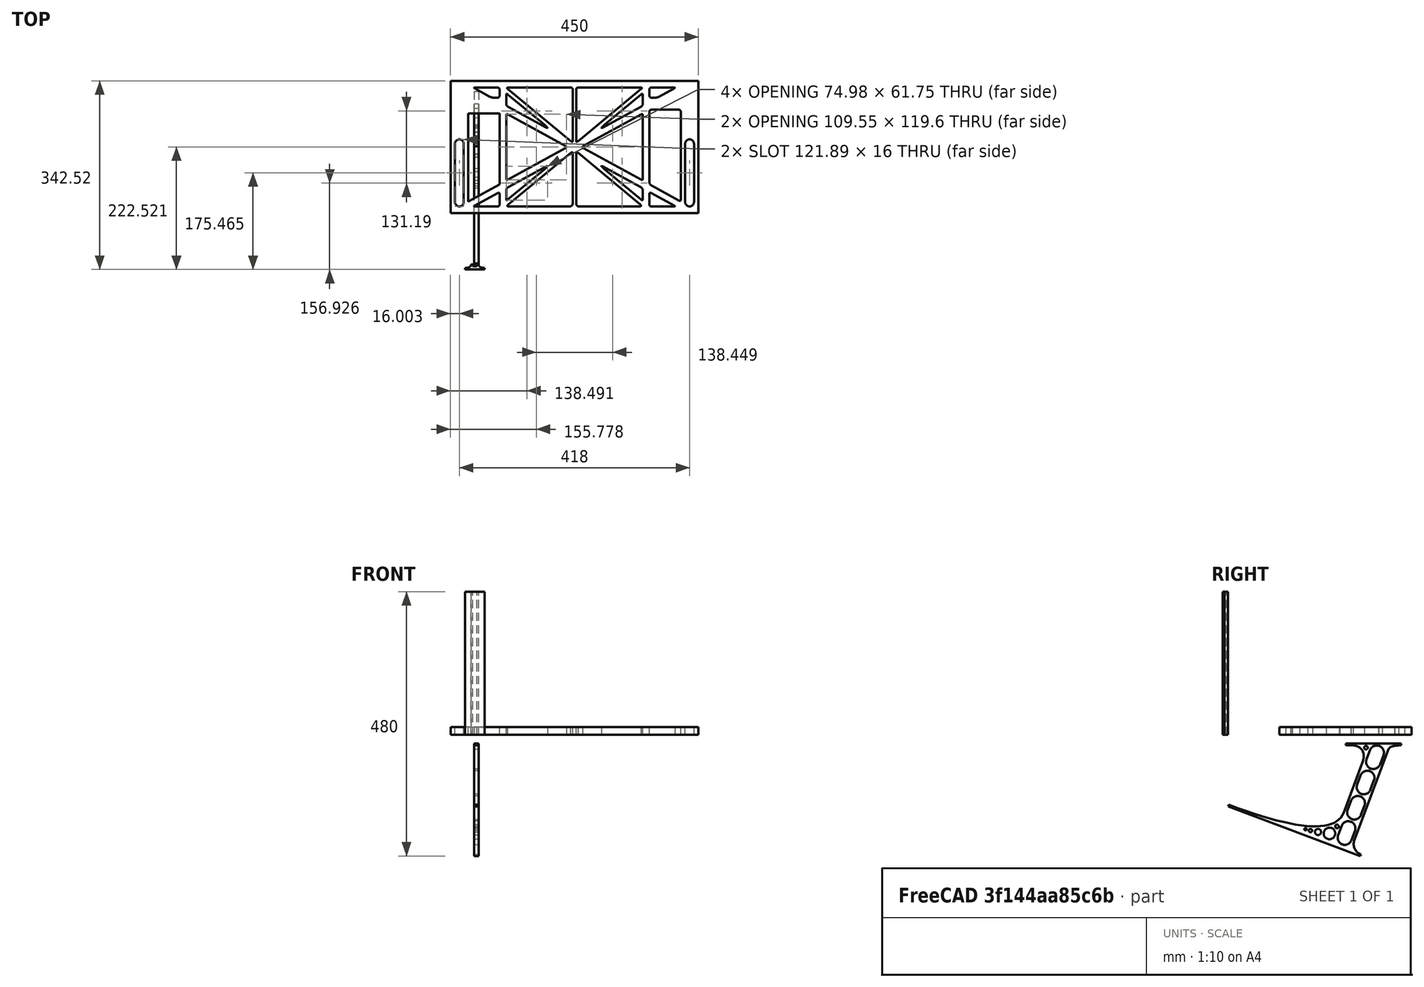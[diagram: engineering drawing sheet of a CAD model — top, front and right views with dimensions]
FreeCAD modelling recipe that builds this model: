
FCSTD DOCUMENT  (FreeCAD 0.19R0.19.2)
Label: laptopStand131FCStd
License: All rights reserved
LicenseURL: http://en.wikipedia.org/wiki/All_rights_reserved
objects: Sketcher::SketchObject×3, Part::Extrusion×3
note: 6 computed .brp shape members not serialized (recipe doc carries the construction recipe); baked Part::Feature solids carry a one-line shape summary decoded from their .brp

FEATURE [Sketcher::SketchObject] Sketch
  FullyConstrained = false
  sketch-geometry (351):
    g0: LineSegment StartX=-10.9272 StartY=-82.7794 StartZ=0 EndX=46.0728 EndY=-51.4823 EndZ=0
    g1: LineSegment StartX=-10.9272 StartY=76.4095 StartZ=0 EndX=-10.9272 EndY=-82.7794 EndZ=0
    g2: LineSegment StartX=46.0728 StartY=76.4095 StartZ=0 EndX=46.0728 EndY=-51.4823 EndZ=0
    g3: LineSegment StartX=-42.9272 StartY=136.221 StartZ=0 EndX=-42.9272 EndY=-103.779 EndZ=0
    g4: LineSegment StartX=407.073 StartY=136.221 StartZ=0 EndX=407.073 EndY=-103.779 EndZ=0
    g5: ArcOfCircle CenterX=-26.9272 CenterY=22.1087 CenterZ=0 NormalX=0 NormalY=0 NormalZ=1 AngleXU=0 Radius=8 StartAngle=1e-16 EndAngle=3.14159
    g6: ArcOfCircle CenterX=-26.9272 CenterY=-83.7794 CenterZ=0 NormalX=0 NormalY=0 NormalZ=1 AngleXU=0 Radius=8 StartAngle=3.14159 EndAngle=6.28319
    g7: LineSegment StartX=-34.9272 StartY=22.1087 StartZ=0 EndX=-34.9272 EndY=-83.7794 EndZ=0
    g8: LineSegment StartX=-18.9272 StartY=22.1087 StartZ=0 EndX=-18.9272 EndY=-83.7794 EndZ=0
    g9: ArcOfCircle CenterX=391.073 CenterY=22.1087 CenterZ=0 NormalX=0 NormalY=0 NormalZ=1 AngleXU=0 Radius=8 StartAngle=-4.4e-15 EndAngle=3.14159
    g10: LineSegment StartX=399.073 StartY=22.1087 StartZ=0 EndX=399.073 EndY=-83.7794 EndZ=0
    g11: LineSegment StartX=383.073 StartY=22.1087 StartZ=0 EndX=383.073 EndY=-83.7794 EndZ=0
    g12: ArcOfCircle CenterX=391.073 CenterY=-83.7794 CenterZ=0 NormalX=0 NormalY=0 NormalZ=1 AngleXU=0 Radius=8 StartAngle=3.14159 EndAngle=6.28319
    g13: Circle CenterX=175.022 CenterY=27.0628 CenterZ=0 NormalX=0 NormalY=0 NormalZ=1 AngleXU=0 Radius=1
    g14: Circle CenterX=179.022 CenterY=24.8665 CenterZ=0 NormalX=0 NormalY=0 NormalZ=1 AngleXU=0 Radius=1
    g15: Circle CenterX=179.022 CenterY=27.0628 CenterZ=0 NormalX=0 NormalY=0 NormalZ=1 AngleXU=0 Radius=1
    g16: BSplineCurve PolesCount=3 KnotsCount=2 Degree=2 IsPeriodic=0
    g17: GeomPoint X=175.022 Y=27.0628 Z=0
    g18: GeomPoint X=179.022 Y=27.0628 Z=0
    g19: Circle CenterX=189.124 CenterY=27.0628 CenterZ=0 NormalX=0 NormalY=0 NormalZ=1 AngleXU=0 Radius=1
    g20: Circle CenterX=185.124 CenterY=24.8665 CenterZ=0 NormalX=0 NormalY=0 NormalZ=1 AngleXU=0 Radius=1
    g21: Circle CenterX=185.124 CenterY=27.0628 CenterZ=0 NormalX=0 NormalY=0 NormalZ=1 AngleXU=0 Radius=1
    g22: BSplineCurve PolesCount=3 KnotsCount=2 Degree=2 IsPeriodic=0
    g23: GeomPoint X=189.124 Y=27.0628 Z=0
    g24: GeomPoint X=185.124 Y=27.0628 Z=0
    g25: Circle CenterX=175.022 CenterY=5.37834 CenterZ=0 NormalX=0 NormalY=0 NormalZ=1 AngleXU=0 Radius=1
    g26: Circle CenterX=179.022 CenterY=7.57463 CenterZ=0 NormalX=0 NormalY=0 NormalZ=1 AngleXU=0 Radius=1
    g27: Circle CenterX=179.022 CenterY=5.34704 CenterZ=0 NormalX=0 NormalY=0 NormalZ=1 AngleXU=0 Radius=1
    g28: BSplineCurve PolesCount=3 KnotsCount=2 Degree=2 IsPeriodic=0
    g29: GeomPoint X=175.022 Y=5.37834 Z=0
    g30: GeomPoint X=179.022 Y=5.34704 Z=0
    g31: Circle CenterX=189.124 CenterY=5.37834 CenterZ=0 NormalX=0 NormalY=0 NormalZ=1 AngleXU=0 Radius=1
    g32: Circle CenterX=185.124 CenterY=7.57463 CenterZ=0 NormalX=0 NormalY=0 NormalZ=1 AngleXU=0 Radius=1
    g33: Circle CenterX=185.124 CenterY=5.34704 CenterZ=0 NormalX=0 NormalY=0 NormalZ=1 AngleXU=0 Radius=1
    g34: BSplineCurve PolesCount=3 KnotsCount=2 Degree=2 IsPeriodic=0
    g35: GeomPoint X=189.124 Y=5.37834 Z=0
    g36: GeomPoint X=185.124 Y=5.34704 Z=0
    g37: Circle CenterX=165.871 CenterY=18.1458 CenterZ=0 NormalX=0 NormalY=0 NormalZ=1 AngleXU=0 Radius=1
    g38: Circle CenterX=169.377 CenterY=16.2206 CenterZ=0 NormalX=0 NormalY=0 NormalZ=1 AngleXU=0 Radius=1
    g39: Circle CenterX=165.871 CenterY=14.2954 CenterZ=0 NormalX=0 NormalY=0 NormalZ=1 AngleXU=0 Radius=1
    g40: BSplineCurve PolesCount=3 KnotsCount=2 Degree=2 IsPeriodic=0
    g41: GeomPoint X=165.871 Y=18.1458 Z=0
    g42: GeomPoint X=165.871 Y=14.2954 Z=0
    g43: Circle CenterX=198.275 CenterY=18.1458 CenterZ=0 NormalX=0 NormalY=0 NormalZ=1 AngleXU=0 Radius=1
    g44: Circle CenterX=194.768 CenterY=16.2206 CenterZ=0 NormalX=0 NormalY=0 NormalZ=1 AngleXU=0 Radius=1
    g45: Circle CenterX=198.275 CenterY=14.2954 CenterZ=0 NormalX=0 NormalY=0 NormalZ=1 AngleXU=0 Radius=1
    g46: BSplineCurve PolesCount=3 KnotsCount=2 Degree=2 IsPeriodic=0
    g47: GeomPoint X=198.275 Y=18.1458 Z=0
    g48: GeomPoint X=198.275 Y=14.2954 Z=0
    g49: LineSegment StartX=407.073 StartY=-103.779 StartZ=0 EndX=-42.9272 EndY=-103.779 EndZ=0
    g50: LineSegment StartX=407.073 StartY=136.221 StartZ=0 EndX=-42.9272 EndY=136.221 EndZ=0
    g51: LineSegment StartX=46.0728 StartY=76.4095 StartZ=0 EndX=-10.9272 EndY=76.4095 EndZ=0
    g52: Circle CenterX=125.607 CenterY=54.1951 CenterZ=0 NormalX=0 NormalY=0 NormalZ=1 AngleXU=0 Radius=1
    g53: Circle CenterX=139.632 CenterY=46.4944 CenterZ=0 NormalX=0 NormalY=0 NormalZ=1 AngleXU=0 Radius=1
    g54: Circle CenterX=127.326 CenterY=56.7187 CenterZ=0 NormalX=0 NormalY=0 NormalZ=1 AngleXU=0 Radius=1
    g55: BSplineCurve PolesCount=3 KnotsCount=2 Degree=2 IsPeriodic=0
    g56: GeomPoint X=125.607 Y=54.1951 Z=0
    g57: GeomPoint X=127.326 Y=56.7187 Z=0
    g58: Circle CenterX=236.821 CenterY=56.7187 CenterZ=0 NormalX=0 NormalY=0 NormalZ=1 AngleXU=0 Radius=1
    g59: Circle CenterX=224.513 CenterY=46.4944 CenterZ=0 NormalX=0 NormalY=0 NormalZ=1 AngleXU=0 Radius=1
    g60: Circle CenterX=238.538 CenterY=54.1951 CenterZ=0 NormalX=0 NormalY=0 NormalZ=1 AngleXU=0 Radius=1
    g61: BSplineCurve PolesCount=3 KnotsCount=2 Degree=2 IsPeriodic=0
    g62: GeomPoint X=236.821 Y=56.7187 Z=0
    g63: GeomPoint X=238.538 Y=54.1951 Z=0
    g64: Circle CenterX=238.538 CenterY=-21.7539 CenterZ=0 NormalX=0 NormalY=0 NormalZ=1 AngleXU=0 Radius=1
    g65: Circle CenterX=224.513 CenterY=-14.0532 CenterZ=0 NormalX=0 NormalY=0 NormalZ=1 AngleXU=0 Radius=1
    g66: Circle CenterX=236.821 CenterY=-24.2775 CenterZ=0 NormalX=0 NormalY=0 NormalZ=1 AngleXU=0 Radius=1
    g67: BSplineCurve PolesCount=3 KnotsCount=2 Degree=2 IsPeriodic=0
    g68: GeomPoint X=238.538 Y=-21.7539 Z=0
    g69: GeomPoint X=236.821 Y=-24.2775 Z=0
    g70: Circle CenterX=125.607 CenterY=-21.7539 CenterZ=0 NormalX=0 NormalY=0 NormalZ=1 AngleXU=0 Radius=1
    g71: Circle CenterX=139.632 CenterY=-14.0532 CenterZ=0 NormalX=0 NormalY=0 NormalZ=1 AngleXU=0 Radius=1
    g72: Circle CenterX=127.325 CenterY=-24.2775 CenterZ=0 NormalX=0 NormalY=0 NormalZ=1 AngleXU=0 Radius=1
    g73: BSplineCurve PolesCount=3 KnotsCount=2 Degree=2 IsPeriodic=0
    g74: GeomPoint X=125.607 Y=-21.7539 Z=0
    g75: GeomPoint X=127.325 Y=-24.2775 Z=0
    g76: Circle CenterX=302.996 CenterY=111.695 CenterZ=0 NormalX=0 NormalY=0 NormalZ=1 AngleXU=0 Radius=1
    g77: Circle CenterX=306.073 CenterY=114.251 CenterZ=0 NormalX=0 NormalY=0 NormalZ=1 AngleXU=0 Radius=1
    g78: Circle CenterX=306.073 CenterY=110.251 CenterZ=0 NormalX=0 NormalY=0 NormalZ=1 AngleXU=0 Radius=1
    g79: BSplineCurve PolesCount=3 KnotsCount=2 Degree=2 IsPeriodic=0
    g80: GeomPoint X=302.996 Y=111.695 Z=0
    g81: GeomPoint X=306.073 Y=110.251 Z=0
    g82: Circle CenterX=306.073 CenterY=95.2763 CenterZ=0 NormalX=0 NormalY=0 NormalZ=1 AngleXU=0 Radius=1
    g83: Circle CenterX=306.073 CenterY=91.2763 CenterZ=0 NormalX=0 NormalY=0 NormalZ=1 AngleXU=0 Radius=1
    g84: Circle CenterX=302.567 CenterY=89.3511 CenterZ=0 NormalX=0 NormalY=0 NormalZ=1 AngleXU=0 Radius=1
    g85: BSplineCurve PolesCount=3 KnotsCount=2 Degree=2 IsPeriodic=0
    g86: GeomPoint X=306.073 Y=95.2763 Z=0
    g87: GeomPoint X=302.567 Y=89.3511 Z=0
    g88: LineSegment StartX=306.073 StartY=110.251 StartZ=0 EndX=306.073 EndY=95.2763 EndZ=0
    g89: LineSegment StartX=302.996 StartY=111.695 StartZ=0 EndX=236.821 EndY=56.7187 EndZ=0
    g90: LineSegment StartX=238.538 StartY=54.1951 StartZ=0 EndX=302.567 EndY=89.3511 EndZ=0
    g91: Circle CenterX=61.1496 CenterY=111.695 CenterZ=0 NormalX=0 NormalY=0 NormalZ=1 AngleXU=0 Radius=1
    g92: Circle CenterX=58.0728 CenterY=114.251 CenterZ=0 NormalX=0 NormalY=0 NormalZ=1 AngleXU=0 Radius=1
    g93: Circle CenterX=58.0728 CenterY=110.251 CenterZ=0 NormalX=0 NormalY=0 NormalZ=1 AngleXU=0 Radius=1
    g94: BSplineCurve PolesCount=3 KnotsCount=2 Degree=2 IsPeriodic=0
    g95: GeomPoint X=61.1496 Y=111.695 Z=0
    g96: GeomPoint X=58.0728 Y=110.251 Z=0
    g97: Circle CenterX=61.5791 CenterY=89.3511 CenterZ=0 NormalX=0 NormalY=0 NormalZ=1 AngleXU=0 Radius=1
    g98: Circle CenterX=58.0728 CenterY=91.2763 CenterZ=0 NormalX=0 NormalY=0 NormalZ=1 AngleXU=0 Radius=1
    g99: Circle CenterX=58.0728 CenterY=95.2763 CenterZ=0 NormalX=0 NormalY=0 NormalZ=1 AngleXU=0 Radius=1
    g100: BSplineCurve PolesCount=3 KnotsCount=2 Degree=2 IsPeriodic=0
    g101: GeomPoint X=61.5791 Y=89.3511 Z=0
    g102: GeomPoint X=58.0728 Y=95.2763 Z=0
    g103: LineSegment StartX=58.0728 StartY=110.251 StartZ=0 EndX=58.0728 EndY=95.2763 EndZ=0
    g104: LineSegment StartX=61.1496 StartY=111.695 StartZ=0 EndX=127.326 EndY=56.7187 EndZ=0
    g105: LineSegment StartX=125.607 StartY=54.1951 StartZ=0 EndX=61.5791 EndY=89.3511 EndZ=0
    g106: Circle CenterX=61.5791 CenterY=-56.9099 CenterZ=0 NormalX=0 NormalY=0 NormalZ=1 AngleXU=0 Radius=1
    g107: Circle CenterX=58.0728 CenterY=-58.8351 CenterZ=0 NormalX=0 NormalY=0 NormalZ=1 AngleXU=0 Radius=1
    g108: Circle CenterX=58.0728 CenterY=-62.8351 CenterZ=0 NormalX=0 NormalY=0 NormalZ=1 AngleXU=0 Radius=1
    g109: BSplineCurve PolesCount=3 KnotsCount=2 Degree=2 IsPeriodic=0
    g110: GeomPoint X=61.5791 Y=-56.9099 Z=0
    g111: GeomPoint X=58.0728 Y=-62.8351 Z=0
    g112: Circle CenterX=58.0728 CenterY=-77.8102 CenterZ=0 NormalX=0 NormalY=0 NormalZ=1 AngleXU=0 Radius=1
    g113: Circle CenterX=58.0728 CenterY=-81.8102 CenterZ=0 NormalX=0 NormalY=0 NormalZ=1 AngleXU=0 Radius=1
    g114: Circle CenterX=61.1496 CenterY=-79.2541 CenterZ=0 NormalX=0 NormalY=0 NormalZ=1 AngleXU=0 Radius=1
    g115: BSplineCurve PolesCount=3 KnotsCount=2 Degree=2 IsPeriodic=0
    g116: GeomPoint X=58.0728 Y=-77.8102 Z=0
    g117: GeomPoint X=61.1496 Y=-79.2541 Z=0
    g118: LineSegment StartX=58.0728 StartY=-62.8351 StartZ=0 EndX=58.0728 EndY=-77.8102 EndZ=0
    g119: LineSegment StartX=61.1496 StartY=-79.2541 StartZ=0 EndX=127.325 EndY=-24.2775 EndZ=0
    g120: LineSegment StartX=125.607 StartY=-21.7539 StartZ=0 EndX=61.5791 EndY=-56.9099 EndZ=0
    g121: Circle CenterX=302.567 CenterY=-56.9099 CenterZ=0 NormalX=0 NormalY=0 NormalZ=1 AngleXU=0 Radius=1
    g122: Circle CenterX=306.073 CenterY=-58.8351 CenterZ=0 NormalX=0 NormalY=0 NormalZ=1 AngleXU=0 Radius=1
    g123: Circle CenterX=306.073 CenterY=-62.8351 CenterZ=0 NormalX=0 NormalY=0 NormalZ=1 AngleXU=0 Radius=1
    g124: BSplineCurve PolesCount=3 KnotsCount=2 Degree=2 IsPeriodic=0
    g125: GeomPoint X=302.567 Y=-56.9099 Z=0
    g126: GeomPoint X=306.073 Y=-62.8351 Z=0
    g127: Circle CenterX=302.996 CenterY=-79.2541 CenterZ=0 NormalX=0 NormalY=0 NormalZ=1 AngleXU=0 Radius=1
    g128: Circle CenterX=306.073 CenterY=-81.8102 CenterZ=0 NormalX=0 NormalY=0 NormalZ=1 AngleXU=0 Radius=1
    g129: Circle CenterX=306.073 CenterY=-77.8102 CenterZ=0 NormalX=0 NormalY=0 NormalZ=1 AngleXU=0 Radius=1
    g130: BSplineCurve PolesCount=3 KnotsCount=2 Degree=2 IsPeriodic=0
    g131: GeomPoint X=302.996 Y=-79.2541 Z=0
    g132: GeomPoint X=306.073 Y=-77.8102 Z=0
    g133: LineSegment StartX=306.073 StartY=-62.8351 StartZ=0 EndX=306.073 EndY=-77.8102 EndZ=0
    g134: LineSegment StartX=302.996 StartY=-79.2541 StartZ=0 EndX=236.821 EndY=-24.2775 EndZ=0
    g135: LineSegment StartX=238.538 StartY=-21.7539 StartZ=0 EndX=302.567 EndY=-56.9099 EndZ=0
    g136: Circle CenterX=61.6457 CenterY=-88.8112 CenterZ=0 NormalX=0 NormalY=0 NormalZ=1 AngleXU=0 Radius=1
    g137: Circle CenterX=58.0728 CenterY=-91.7794 CenterZ=0 NormalX=0 NormalY=0 NormalZ=1 AngleXU=0 Radius=1
    g138: Circle CenterX=63.9135 CenterY=-91.7794 CenterZ=0 NormalX=0 NormalY=0 NormalZ=1 AngleXU=0 Radius=1
    g139: BSplineCurve PolesCount=3 KnotsCount=2 Degree=2 IsPeriodic=0
    g140: GeomPoint X=61.6457 Y=-88.8112 Z=0
    g141: GeomPoint X=63.9135 Y=-91.7794 Z=0
    g142: Circle CenterX=179.022 CenterY=-85.8163 CenterZ=0 NormalX=0 NormalY=0 NormalZ=1 AngleXU=0 Radius=1
    g143: Circle CenterX=179.022 CenterY=-91.7794 CenterZ=0 NormalX=0 NormalY=0 NormalZ=1 AngleXU=0 Radius=1
    g144: Circle CenterX=171.895 CenterY=-91.7794 CenterZ=0 NormalX=0 NormalY=0 NormalZ=1 AngleXU=0 Radius=1
    g145: BSplineCurve PolesCount=3 KnotsCount=2 Degree=2 IsPeriodic=0
    g146: GeomPoint X=179.022 Y=-85.8163 Z=0
    g147: GeomPoint X=171.895 Y=-91.7794 Z=0
    g148: Circle CenterX=185.124 CenterY=-86.2028 CenterZ=0 NormalX=0 NormalY=0 NormalZ=1 AngleXU=0 Radius=1
    g149: Circle CenterX=185.124 CenterY=-91.7794 CenterZ=0 NormalX=0 NormalY=0 NormalZ=1 AngleXU=0 Radius=1
    g150: Circle CenterX=191.747 CenterY=-91.7794 CenterZ=0 NormalX=0 NormalY=0 NormalZ=1 AngleXU=0 Radius=1
    g151: BSplineCurve PolesCount=3 KnotsCount=2 Degree=2 IsPeriodic=0
    g152: GeomPoint X=185.124 Y=-86.2028 Z=0
    g153: GeomPoint X=191.747 Y=-91.7794 Z=0
    g154: Circle CenterX=299.888 CenterY=-86.6413 CenterZ=0 NormalX=0 NormalY=0 NormalZ=1 AngleXU=0 Radius=1
    g155: Circle CenterX=306.073 CenterY=-91.7794 CenterZ=0 NormalX=0 NormalY=0 NormalZ=1 AngleXU=0 Radius=1
    g156: Circle CenterX=298.776 CenterY=-91.7794 CenterZ=0 NormalX=0 NormalY=0 NormalZ=1 AngleXU=0 Radius=1
    g157: BSplineCurve PolesCount=3 KnotsCount=2 Degree=2 IsPeriodic=0
    g158: GeomPoint X=299.888 Y=-86.6413 Z=0
    g159: GeomPoint X=298.776 Y=-91.7794 Z=0
    g160: LineSegment StartX=189.124 StartY=5.37834 StartZ=0 EndX=299.888 EndY=-86.6413 EndZ=0
    g161: LineSegment StartX=298.776 StartY=-91.7794 StartZ=0 EndX=191.747 EndY=-91.7794 EndZ=0
    g162: LineSegment StartX=185.124 StartY=-86.2028 StartZ=0 EndX=185.124 EndY=5.34704 EndZ=0
    g163: LineSegment StartX=179.022 StartY=5.34704 StartZ=0 EndX=179.022 EndY=-85.8163 EndZ=0
    g164: LineSegment StartX=171.895 StartY=-91.7794 StartZ=0 EndX=63.9135 EndY=-91.7794 EndZ=0
    g165: LineSegment StartX=61.6457 StartY=-88.8112 StartZ=0 EndX=175.022 EndY=5.37834 EndZ=0
    g166: Circle CenterX=302.073 CenterY=124.221 CenterZ=0 NormalX=0 NormalY=0 NormalZ=1 AngleXU=0 Radius=1
    g167: Circle CenterX=306.073 CenterY=124.221 CenterZ=0 NormalX=0 NormalY=0 NormalZ=1 AngleXU=0 Radius=1
    g168: Circle CenterX=302.996 CenterY=121.665 CenterZ=0 NormalX=0 NormalY=0 NormalZ=1 AngleXU=0 Radius=1
    g169: BSplineCurve PolesCount=3 KnotsCount=2 Degree=2 IsPeriodic=0
    g170: GeomPoint X=302.073 Y=124.221 Z=0
    g171: GeomPoint X=302.996 Y=121.665 Z=0
    g172: Circle CenterX=189.124 CenterY=124.221 CenterZ=0 NormalX=0 NormalY=0 NormalZ=1 AngleXU=0 Radius=1
    g173: Circle CenterX=185.124 CenterY=124.221 CenterZ=0 NormalX=0 NormalY=0 NormalZ=1 AngleXU=0 Radius=1
    g174: Circle CenterX=185.124 CenterY=120.221 CenterZ=0 NormalX=0 NormalY=0 NormalZ=1 AngleXU=0 Radius=1
    g175: BSplineCurve PolesCount=3 KnotsCount=2 Degree=2 IsPeriodic=0
    g176: GeomPoint X=189.124 Y=124.221 Z=0
    g177: GeomPoint X=185.124 Y=120.221 Z=0
    g178: Circle CenterX=175.022 CenterY=124.221 CenterZ=0 NormalX=0 NormalY=0 NormalZ=1 AngleXU=0 Radius=1
    g179: Circle CenterX=179.022 CenterY=124.221 CenterZ=0 NormalX=0 NormalY=0 NormalZ=1 AngleXU=0 Radius=1
    g180: Circle CenterX=179.022 CenterY=120.221 CenterZ=0 NormalX=0 NormalY=0 NormalZ=1 AngleXU=0 Radius=1
    g181: BSplineCurve PolesCount=3 KnotsCount=2 Degree=2 IsPeriodic=0
    g182: GeomPoint X=175.022 Y=124.221 Z=0
    g183: GeomPoint X=179.022 Y=120.221 Z=0
    g184: Circle CenterX=62.0728 CenterY=124.221 CenterZ=0 NormalX=0 NormalY=0 NormalZ=1 AngleXU=0 Radius=1
    g185: Circle CenterX=58.0728 CenterY=124.221 CenterZ=0 NormalX=0 NormalY=0 NormalZ=1 AngleXU=0 Radius=1
    g186: Circle CenterX=61.1496 CenterY=121.665 CenterZ=0 NormalX=0 NormalY=0 NormalZ=1 AngleXU=0 Radius=1
    g187: BSplineCurve PolesCount=3 KnotsCount=2 Degree=2 IsPeriodic=0
    g188: GeomPoint X=62.0728 Y=124.221 Z=0
    g189: GeomPoint X=61.1496 Y=121.665 Z=0
    g190: LineSegment StartX=62.0728 StartY=124.221 StartZ=0 EndX=175.022 EndY=124.221 EndZ=0
    g191: LineSegment StartX=179.022 StartY=120.221 StartZ=0 EndX=179.022 EndY=27.0628 EndZ=0
    g192: LineSegment StartX=185.124 StartY=27.0628 StartZ=0 EndX=185.124 EndY=120.221 EndZ=0
    g193: LineSegment StartX=189.124 StartY=124.221 StartZ=0 EndX=302.073 EndY=124.221 EndZ=0
    g194: LineSegment StartX=302.996 StartY=121.665 StartZ=0 EndX=189.124 EndY=27.0628 EndZ=0
    g195: LineSegment StartX=175.022 StartY=27.0628 StartZ=0 EndX=61.1496 EndY=121.665 EndZ=0
    g196: Circle CenterX=61.5791 CenterY=75.4095 CenterZ=0 NormalX=0 NormalY=0 NormalZ=1 AngleXU=0 Radius=1
    g197: Circle CenterX=58.0728 CenterY=77.3346 CenterZ=0 NormalX=0 NormalY=0 NormalZ=1 AngleXU=0 Radius=1
    g198: Circle CenterX=58.0728 CenterY=73.3346 CenterZ=0 NormalX=0 NormalY=0 NormalZ=1 AngleXU=0 Radius=1
    g199: BSplineCurve PolesCount=3 KnotsCount=2 Degree=2 IsPeriodic=0
    g200: GeomPoint X=61.5791 Y=75.4095 Z=0
    g201: GeomPoint X=58.0728 Y=73.3346 Z=0
    g202: Circle CenterX=58.0728 CenterY=-40.8935 CenterZ=0 NormalX=0 NormalY=0 NormalZ=1 AngleXU=0 Radius=1
    g203: Circle CenterX=58.0728 CenterY=-44.8935 CenterZ=0 NormalX=0 NormalY=0 NormalZ=1 AngleXU=0 Radius=1
    g204: Circle CenterX=61.5791 CenterY=-42.9683 CenterZ=0 NormalX=0 NormalY=0 NormalZ=1 AngleXU=0 Radius=1
    g205: BSplineCurve PolesCount=3 KnotsCount=2 Degree=2 IsPeriodic=0
    g206: GeomPoint X=58.0728 Y=-40.8935 Z=0
    g207: GeomPoint X=61.5791 Y=-42.9683 Z=0
    g208: LineSegment StartX=61.5791 StartY=-42.9683 StartZ=0 EndX=165.871 EndY=14.2954 EndZ=0
    g209: LineSegment StartX=165.871 StartY=18.1458 StartZ=0 EndX=61.5791 EndY=75.4095 EndZ=0
    g210: LineSegment StartX=58.0728 StartY=73.3346 StartZ=0 EndX=58.0728 EndY=-40.8935 EndZ=0
    g211: Circle CenterX=302.567 CenterY=-42.9683 CenterZ=0 NormalX=0 NormalY=0 NormalZ=1 AngleXU=0 Radius=1
    g212: Circle CenterX=306.073 CenterY=-44.8935 CenterZ=0 NormalX=0 NormalY=0 NormalZ=1 AngleXU=0 Radius=1
    g213: Circle CenterX=306.073 CenterY=-40.8935 CenterZ=0 NormalX=0 NormalY=0 NormalZ=1 AngleXU=0 Radius=1
    g214: BSplineCurve PolesCount=3 KnotsCount=2 Degree=2 IsPeriodic=0
    g215: GeomPoint X=302.567 Y=-42.9683 Z=0
    g216: GeomPoint X=306.073 Y=-40.8935 Z=0
    g217: Circle CenterX=306.073 CenterY=73.3346 CenterZ=0 NormalX=0 NormalY=0 NormalZ=1 AngleXU=0 Radius=1
    g218: Circle CenterX=306.073 CenterY=77.3346 CenterZ=0 NormalX=0 NormalY=0 NormalZ=1 AngleXU=0 Radius=1
    g219: Circle CenterX=302.567 CenterY=75.4095 CenterZ=0 NormalX=0 NormalY=0 NormalZ=1 AngleXU=0 Radius=1
    g220: BSplineCurve PolesCount=3 KnotsCount=2 Degree=2 IsPeriodic=0
    g221: GeomPoint X=306.073 Y=73.3346 Z=0
    g222: GeomPoint X=302.567 Y=75.4095 Z=0
    g223: LineSegment StartX=302.567 StartY=-42.9683 StartZ=0 EndX=198.275 EndY=14.2954 EndZ=0
    g224: LineSegment StartX=198.275 StartY=18.1458 StartZ=0 EndX=302.567 EndY=75.4095 EndZ=0
    g225: LineSegment StartX=306.073 StartY=73.3346 StartZ=0 EndX=306.073 EndY=-40.8935 EndZ=0
    g226: LineSegment StartX=322.073 StartY=105.865 StartZ=0 EndX=328.643 EndY=105.865 EndZ=0
    g227: LineSegment StartX=318.073 StartY=120.221 StartZ=0 EndX=318.073 EndY=109.865 EndZ=0
    g228: LineSegment StartX=336.157 StartY=107.779 StartZ=0 EndX=362.567 EndY=122.294 EndZ=0
    g229: Circle CenterX=362.073 CenterY=124.221 CenterZ=0 NormalX=0 NormalY=0 NormalZ=1 AngleXU=0 Radius=1
    g230: Circle CenterX=366.073 CenterY=124.221 CenterZ=0 NormalX=0 NormalY=0 NormalZ=1 AngleXU=0 Radius=1
    g231: Circle CenterX=362.567 CenterY=122.294 CenterZ=0 NormalX=0 NormalY=0 NormalZ=1 AngleXU=0 Radius=1
    g232: BSplineCurve PolesCount=3 KnotsCount=2 Degree=2 IsPeriodic=0
    g233: GeomPoint X=362.073 Y=124.221 Z=0
    g234: GeomPoint X=362.567 Y=122.294 Z=0
    g235: Circle CenterX=322.073 CenterY=124.221 CenterZ=0 NormalX=0 NormalY=0 NormalZ=1 AngleXU=0 Radius=1
    g236: Circle CenterX=318.073 CenterY=124.221 CenterZ=0 NormalX=0 NormalY=0 NormalZ=1 AngleXU=0 Radius=1
    g237: Circle CenterX=318.073 CenterY=120.221 CenterZ=0 NormalX=0 NormalY=0 NormalZ=1 AngleXU=0 Radius=1
    g238: BSplineCurve PolesCount=3 KnotsCount=2 Degree=2 IsPeriodic=0
    g239: GeomPoint X=322.073 Y=124.221 Z=0
    g240: GeomPoint X=318.073 Y=120.221 Z=0
    g241: Circle CenterX=322.073 CenterY=105.865 CenterZ=0 NormalX=0 NormalY=0 NormalZ=1 AngleXU=0 Radius=1
    g242: Circle CenterX=318.073 CenterY=105.865 CenterZ=0 NormalX=0 NormalY=0 NormalZ=1 AngleXU=0 Radius=1
    g243: Circle CenterX=318.073 CenterY=109.865 CenterZ=0 NormalX=0 NormalY=0 NormalZ=1 AngleXU=0 Radius=1
    g244: BSplineCurve PolesCount=3 KnotsCount=2 Degree=2 IsPeriodic=0
    g245: GeomPoint X=322.073 Y=105.865 Z=0
    g246: GeomPoint X=318.073 Y=109.865 Z=0
    g247: Circle CenterX=336.157 CenterY=107.779 CenterZ=0 NormalX=0 NormalY=0 NormalZ=1 AngleXU=0 Radius=1
    g248: Circle CenterX=332.651 CenterY=105.853 CenterZ=0 NormalX=0 NormalY=0 NormalZ=1 AngleXU=0 Radius=1
    g249: Circle CenterX=328.643 CenterY=105.865 CenterZ=0 NormalX=0 NormalY=0 NormalZ=1 AngleXU=0 Radius=1
    g250: BSplineCurve PolesCount=3 KnotsCount=2 Degree=2 IsPeriodic=0
    g251: GeomPoint X=336.157 Y=107.779 Z=0
    g252: GeomPoint X=328.643 Y=105.865 Z=0
    g253: LineSegment StartX=322.073 StartY=124.221 StartZ=0 EndX=362.073 EndY=124.221 EndZ=0
    g254: Circle CenterX=371.567 CenterY=-80.8644 CenterZ=0 NormalX=0 NormalY=0 NormalZ=1 AngleXU=0 Radius=1
    g255: Circle CenterX=375.073 CenterY=-82.7896 CenterZ=0 NormalX=0 NormalY=0 NormalZ=1 AngleXU=0 Radius=1
    g256: Circle CenterX=375.073 CenterY=-78.7896 CenterZ=0 NormalX=0 NormalY=0 NormalZ=1 AngleXU=0 Radius=1
    g257: BSplineCurve PolesCount=3 KnotsCount=2 Degree=2 IsPeriodic=0
    g258: GeomPoint X=371.567 Y=-80.8644 Z=0
    g259: GeomPoint X=375.073 Y=-78.7896 Z=0
    g260: Circle CenterX=321.579 CenterY=-53.4075 CenterZ=0 NormalX=0 NormalY=0 NormalZ=1 AngleXU=0 Radius=1
    g261: Circle CenterX=318.073 CenterY=-51.4823 CenterZ=0 NormalX=0 NormalY=0 NormalZ=1 AngleXU=0 Radius=1
    g262: Circle CenterX=318.073 CenterY=-47.4823 CenterZ=0 NormalX=0 NormalY=0 NormalZ=1 AngleXU=0 Radius=1
    g263: BSplineCurve PolesCount=3 KnotsCount=2 Degree=2 IsPeriodic=0
    g264: GeomPoint X=321.579 Y=-53.4075 Z=0
    g265: GeomPoint X=318.073 Y=-47.4823 Z=0
    g266: Circle CenterX=375.073 CenterY=79.9235 CenterZ=0 NormalX=0 NormalY=0 NormalZ=1 AngleXU=0 Radius=1
    g267: Circle CenterX=375.073 CenterY=83.9235 CenterZ=0 NormalX=0 NormalY=0 NormalZ=1 AngleXU=0 Radius=1
    g268: Circle CenterX=371.073 CenterY=83.9235 CenterZ=0 NormalX=0 NormalY=0 NormalZ=1 AngleXU=0 Radius=1
    g269: BSplineCurve PolesCount=3 KnotsCount=2 Degree=2 IsPeriodic=0
    g270: GeomPoint X=375.073 Y=79.9235 Z=0
    g271: GeomPoint X=371.073 Y=83.9235 Z=0
    g272: LineSegment StartX=371.567 StartY=-80.8644 StartZ=0 EndX=321.579 EndY=-53.4075 EndZ=0
    g273: LineSegment StartX=318.073 StartY=-47.4823 StartZ=0 EndX=318.073 EndY=76.4095 EndZ=0
    g274: Circle CenterX=321.579 CenterY=-67.3492 CenterZ=0 NormalX=0 NormalY=0 NormalZ=1 AngleXU=0 Radius=1
    g275: Circle CenterX=318.073 CenterY=-65.424 CenterZ=0 NormalX=0 NormalY=0 NormalZ=1 AngleXU=0 Radius=1
    g276: Circle CenterX=318.073 CenterY=-69.424 CenterZ=0 NormalX=0 NormalY=0 NormalZ=1 AngleXU=0 Radius=1
    g277: BSplineCurve PolesCount=3 KnotsCount=2 Degree=2 IsPeriodic=0
    g278: GeomPoint X=321.579 Y=-67.3492 Z=0
    g279: GeomPoint X=318.073 Y=-69.424 Z=0
    g280: Circle CenterX=362.567 CenterY=-89.8542 CenterZ=0 NormalX=0 NormalY=0 NormalZ=1 AngleXU=0 Radius=1
    g281: Circle CenterX=366.073 CenterY=-91.7794 CenterZ=0 NormalX=0 NormalY=0 NormalZ=1 AngleXU=0 Radius=1
    g282: Circle CenterX=362.073 CenterY=-91.7794 CenterZ=0 NormalX=0 NormalY=0 NormalZ=1 AngleXU=0 Radius=1
    g283: BSplineCurve PolesCount=3 KnotsCount=2 Degree=2 IsPeriodic=0
    g284: GeomPoint X=362.567 Y=-89.8542 Z=0
    g285: GeomPoint X=362.073 Y=-91.7794 Z=0
    g286: Circle CenterX=322.073 CenterY=-91.7794 CenterZ=0 NormalX=0 NormalY=0 NormalZ=1 AngleXU=0 Radius=1
    g287: Circle CenterX=318.073 CenterY=-91.7794 CenterZ=0 NormalX=0 NormalY=0 NormalZ=1 AngleXU=0 Radius=1
    g288: Circle CenterX=318.073 CenterY=-87.7794 CenterZ=0 NormalX=0 NormalY=0 NormalZ=1 AngleXU=0 Radius=1
    g289: BSplineCurve PolesCount=3 KnotsCount=2 Degree=2 IsPeriodic=0
    g290: GeomPoint X=322.073 Y=-91.7794 Z=0
    g291: GeomPoint X=318.073 Y=-87.7794 Z=0
    g292: LineSegment StartX=362.567 StartY=-89.8542 StartZ=0 EndX=321.579 EndY=-67.3492 EndZ=0
    g293: LineSegment StartX=318.073 StartY=-69.424 StartZ=0 EndX=318.073 EndY=-87.7794 EndZ=0
    g294: LineSegment StartX=322.073 StartY=-91.7794 StartZ=0 EndX=362.073 EndY=-91.7794 EndZ=0
    g295: Circle CenterX=2.07281 CenterY=124.221 CenterZ=0 NormalX=0 NormalY=0 NormalZ=1 AngleXU=0 Radius=1
    g296: Circle CenterX=1.57905 CenterY=122.295 CenterZ=0 NormalX=0 NormalY=0 NormalZ=1 AngleXU=0 Radius=1
    g297: BSplineCurve PolesCount=3 KnotsCount=2 Degree=2 IsPeriodic=0
    g298: GeomPoint X=2.07281 Y=124.221 Z=0
    g299: GeomPoint X=1.57905 Y=122.295 Z=0
    g300: Circle CenterX=42.0728 CenterY=124.221 CenterZ=0 NormalX=0 NormalY=0 NormalZ=1 AngleXU=0 Radius=1
    g301: Circle CenterX=46.0728 CenterY=124.221 CenterZ=0 NormalX=0 NormalY=0 NormalZ=1 AngleXU=0 Radius=1
    g302: Circle CenterX=46.0728 CenterY=120.221 CenterZ=0 NormalX=0 NormalY=0 NormalZ=1 AngleXU=0 Radius=1
    g303: BSplineCurve PolesCount=3 KnotsCount=2 Degree=2 IsPeriodic=0
    g304: GeomPoint X=42.0728 Y=124.221 Z=0
    g305: GeomPoint X=46.0728 Y=120.221 Z=0
    g306: Circle CenterX=46.0728 CenterY=109.865 CenterZ=0 NormalX=0 NormalY=0 NormalZ=1 AngleXU=0 Radius=1
    g307: Circle CenterX=46.0728 CenterY=105.865 CenterZ=0 NormalX=0 NormalY=0 NormalZ=1 AngleXU=0 Radius=1
    g308: Circle CenterX=42.0728 CenterY=105.865 CenterZ=0 NormalX=0 NormalY=0 NormalZ=1 AngleXU=0 Radius=1
    g309: BSplineCurve PolesCount=3 KnotsCount=2 Degree=2 IsPeriodic=0
    g310: GeomPoint X=46.0728 Y=109.865 Z=0
    g311: GeomPoint X=42.0728 Y=105.865 Z=0
    g312: Circle CenterX=35.5028 CenterY=105.865 CenterZ=0 NormalX=0 NormalY=0 NormalZ=1 AngleXU=0 Radius=1
    g313: Circle CenterX=31.5028 CenterY=105.865 CenterZ=0 NormalX=0 NormalY=0 NormalZ=1 AngleXU=0 Radius=1
    g314: Circle CenterX=27.9965 CenterY=107.79 CenterZ=0 NormalX=0 NormalY=0 NormalZ=1 AngleXU=0 Radius=1
    g315: BSplineCurve PolesCount=3 KnotsCount=2 Degree=2 IsPeriodic=0
    g316: GeomPoint X=35.5028 Y=105.865 Z=0
    g317: GeomPoint X=27.9965 Y=107.79 Z=0
    g318: LineSegment StartX=2.07281 StartY=124.221 StartZ=0 EndX=42.0728 EndY=124.221 EndZ=0
    g319: LineSegment StartX=46.0728 StartY=120.221 StartZ=0 EndX=46.0728 EndY=109.865 EndZ=0
    g320: LineSegment StartX=42.0728 StartY=105.865 StartZ=0 EndX=35.5028 EndY=105.865 EndZ=0
    g321: LineSegment StartX=27.9965 StartY=107.79 StartZ=0 EndX=1.57905 EndY=122.295 EndZ=0
    g322: Circle CenterX=42.5666 CenterY=-67.3492 CenterZ=0 NormalX=0 NormalY=0 NormalZ=1 AngleXU=0 Radius=1
    g323: Circle CenterX=46.0728 CenterY=-65.424 CenterZ=0 NormalX=0 NormalY=0 NormalZ=1 AngleXU=0 Radius=1
    g324: Circle CenterX=46.0728 CenterY=-69.424 CenterZ=0 NormalX=0 NormalY=0 NormalZ=1 AngleXU=0 Radius=1
    g325: BSplineCurve PolesCount=3 KnotsCount=2 Degree=2 IsPeriodic=0
    g326: GeomPoint X=42.5666 Y=-67.3492 Z=0
    g327: GeomPoint X=46.0728 Y=-69.424 Z=0
    g328: Circle CenterX=46.0728 CenterY=-87.7794 CenterZ=0 NormalX=0 NormalY=0 NormalZ=1 AngleXU=0 Radius=1
    g329: Circle CenterX=46.0728 CenterY=-91.7794 CenterZ=0 NormalX=0 NormalY=0 NormalZ=1 AngleXU=0 Radius=1
    g330: Circle CenterX=42.0728 CenterY=-91.7794 CenterZ=0 NormalX=0 NormalY=0 NormalZ=1 AngleXU=0 Radius=1
    g331: BSplineCurve PolesCount=3 KnotsCount=2 Degree=2 IsPeriodic=0
    g332: GeomPoint X=46.0728 Y=-87.7794 Z=0
    g333: GeomPoint X=42.0728 Y=-91.7794 Z=0
    g334: Circle CenterX=2.07281 CenterY=-91.7794 CenterZ=0 NormalX=0 NormalY=0 NormalZ=1 AngleXU=0 Radius=1
    g335: Circle CenterX=-1.92719 CenterY=-91.7794 CenterZ=0 NormalX=0 NormalY=0 NormalZ=1 AngleXU=0 Radius=1
    g336: Circle CenterX=1.57905 CenterY=-89.8542 CenterZ=0 NormalX=0 NormalY=0 NormalZ=1 AngleXU=0 Radius=1
    g337: BSplineCurve PolesCount=3 KnotsCount=2 Degree=2 IsPeriodic=0
    g338: GeomPoint X=2.07281 Y=-91.7794 Z=0
    g339: GeomPoint X=1.57905 Y=-89.8542 Z=0
    g340: LineSegment StartX=2.07281 StartY=-91.7794 StartZ=0 EndX=42.0728 EndY=-91.7794 EndZ=0
    g341: LineSegment StartX=46.0728 StartY=-87.7794 StartZ=0 EndX=46.0728 EndY=-69.424 EndZ=0
    g342: LineSegment StartX=42.5666 StartY=-67.3492 StartZ=0 EndX=1.57905 EndY=-89.8542 EndZ=0
    g343: LineSegment StartX=318.073 StartY=76.4095 StartZ=0 EndX=375.073 EndY=76.4095 EndZ=0
    g344: LineSegment StartX=375.073 StartY=76.4095 StartZ=0 EndX=375.073 EndY=-78.7896 EndZ=0
    g345: LineSegment StartX=318.073 StartY=76.4095 StartZ=0 EndX=322.073 EndY=76.4095 EndZ=0
    g346: Circle CenterX=322.073 CenterY=76.4095 CenterZ=0 NormalX=0 NormalY=0 NormalZ=1 AngleXU=0 Radius=1
    g347: BSplineCurve PolesCount=3 KnotsCount=2 Degree=2 IsPeriodic=0
    g348: GeomPoint X=318.073 Y=72.4095 Z=0
    g349: GeomPoint X=322.073 Y=76.4095 Z=0
    g350: LineSegment StartX=370.522 StartY=78.4793 StartZ=0 EndX=374.522 EndY=78.4793 EndZ=0
  constraints (580):
    c: Coincident(g0,g2)
    c: Block(g0)
    c: Block(g1)
    c: Vertical(g3)
    c: Vertical(g4)
    c: Block(g4)
    c: Block(g3)
    c: Tangent(g5,g8) = 1.5708
    c: Tangent(g5,g7) = -1.5708
    c: Tangent(g7,g6) = -1.5708
    c: Tangent(g8,g6) = 1.5708
    c: Vertical(g7)
    c: Equal(g5,g6)
    c: Block(g8)
    c: Block(g7)
    c: Tangent(g9,g10) = 1.5708
    c: Tangent(g10,g12) = 1.5708
    c: Equal(g9,g12)
    c: Coincident(g11,g9)
    c: Coincident(g11,g12)
    c: Block(g10)
    c: Block(g11)
    c: Weight(g13) = 1
    c: Equal(g13,g14)
    c: Equal(g13,g15)
    c: InternalAlignment(g13,g16)
    c: InternalAlignment(g14,g16)
    c: InternalAlignment(g15,g16)
    c: InternalAlignment(g17,g16)
    c: InternalAlignment(g18,g16)
    c: Weight(g19) = 1
    c: Equal(g19,g20)
    c: Equal(g19,g21)
    c: InternalAlignment(g19,g22)
    c: InternalAlignment(g20,g22)
    c: InternalAlignment(g21,g22)
    c: InternalAlignment(g23,g22)
    c: InternalAlignment(g24,g22)
    c: Block(g22)
    c: Block(g16)
    c: Weight(g25) = 1
    c: Equal(g25,g26)
    c: Equal(g25,g27)
    c: InternalAlignment(g25,g28)
    c: InternalAlignment(g26,g28)
    c: InternalAlignment(g27,g28)
    c: InternalAlignment(g29,g28)
    c: InternalAlignment(g30,g28)
    c: Weight(g31) = 1
    c: Equal(g31,g32)
    c: Equal(g31,g33)
    c: InternalAlignment(g31,g34)
    c: InternalAlignment(g32,g34)
    c: InternalAlignment(g33,g34)
    c: InternalAlignment(g35,g34)
    c: InternalAlignment(g36,g34)
    c: Block(g34)
    c: Block(g28)
    c: Weight(g37) = 1
    c: Equal(g37,g38)
    c: Equal(g37,g39)
    c: InternalAlignment(g37,g40)
    c: InternalAlignment(g38,g40)
    c: InternalAlignment(g39,g40)
    c: InternalAlignment(g41,g40)
    c: InternalAlignment(g42,g40)
    c: Weight(g43) = 1
    c: Equal(g43,g44)
    c: Equal(g43,g45)
    c: InternalAlignment(g43,g46)
    c: InternalAlignment(g44,g46)
    c: InternalAlignment(g45,g46)
    c: InternalAlignment(g47,g46)
    c: InternalAlignment(g48,g46)
    c: Block(g40)
    c: Block(g46)
    c: Coincident(g49,g4)
    c: Coincident(g49,g3)
    c: Horizontal(g49)
    c: Distance(g49) = 450
    c: Coincident(g50,g4)
    c: Coincident(g50,g3)
    c: Horizontal(g50)
    c: Horizontal(g51)
    c: Coincident(g2,g51)
    c: Block(g51)
    c: Coincident(g1,g51)
    c: Weight(g52) = 1
    c: Equal(g52,g53)
    c: Equal(g52,g54)
    c: InternalAlignment(g52,g55)
    c: InternalAlignment(g53,g55)
    c: InternalAlignment(g54,g55)
    c: InternalAlignment(g56,g55)
    c: InternalAlignment(g57,g55)
    c: Block(g55)
    c: Weight(g58) = 1
    c: Equal(g58,g59)
    c: Equal(g58,g60)
    c: InternalAlignment(g58,g61)
    c: InternalAlignment(g59,g61)
    c: InternalAlignment(g60,g61)
    c: InternalAlignment(g62,g61)
    c: InternalAlignment(g63,g61)
    c: Block(g61)
    c: Weight(g64) = 1
    c: Equal(g64,g65)
    c: Equal(g64,g66)
    c: InternalAlignment(g64,g67)
    c: InternalAlignment(g65,g67)
    c: InternalAlignment(g66,g67)
    c: InternalAlignment(g68,g67)
    c: InternalAlignment(g69,g67)
    c: Block(g67)
    c: Weight(g70) = 1
    c: Equal(g70,g71)
    c: Equal(g70,g72)
    c: InternalAlignment(g70,g73)
    c: InternalAlignment(g71,g73)
    c: InternalAlignment(g72,g73)
    c: InternalAlignment(g74,g73)
    c: InternalAlignment(g75,g73)
    c: Block(g73)
    c: Weight(g76) = 1
    c: Equal(g76,g77)
    c: Equal(g76,g78)
    c: InternalAlignment(g76,g79)
    c: InternalAlignment(g77,g79)
    c: InternalAlignment(g78,g79)
    c: InternalAlignment(g80,g79)
    c: InternalAlignment(g81,g79)
    c: Weight(g82) = 1
    c: Equal(g82,g83)
    c: Equal(g82,g84)
    c: InternalAlignment(g82,g85)
    c: InternalAlignment(g83,g85)
    c: InternalAlignment(g84,g85)
    c: InternalAlignment(g86,g85)
    c: InternalAlignment(g87,g85)
    c: Block(g79)
    c: Block(g85)
    c: Coincident(g88,g79)
    c: Coincident(g88,g85)
    c: Vertical(g88)
    c: Coincident(g89,g79)
    c: Coincident(g89,g61)
    c: Coincident(g90,g61)
    c: Coincident(g90,g85)
    c: Weight(g91) = 1
    c: Equal(g91,g92)
    c: Equal(g91,g93)
    c: InternalAlignment(g91,g94)
    c: InternalAlignment(g92,g94)
    c: InternalAlignment(g93,g94)
    c: InternalAlignment(g95,g94)
    c: InternalAlignment(g96,g94)
    c: Weight(g97) = 1
    c: Equal(g97,g98)
    c: Equal(g97,g99)
    c: InternalAlignment(g97,g100)
    c: InternalAlignment(g98,g100)
    c: InternalAlignment(g99,g100)
    c: InternalAlignment(g101,g100)
    c: InternalAlignment(g102,g100)
    c: Block(g94)
    c: Block(g100)
    c: Coincident(g103,g94)
    c: Coincident(g103,g100)
    c: Vertical(g103)
    c: Coincident(g104,g94)
    c: Coincident(g104,g55)
    c: Coincident(g105,g55)
    c: Coincident(g105,g100)
    c: Weight(g106) = 1
    c: Equal(g106,g107)
    c: Equal(g106,g108)
    c: InternalAlignment(g106,g109)
    c: InternalAlignment(g107,g109)
    c: InternalAlignment(g108,g109)
    c: InternalAlignment(g110,g109)
    c: InternalAlignment(g111,g109)
    c: Weight(g112) = 1
    c: Equal(g112,g113)
    c: Equal(g112,g114)
    c: InternalAlignment(g112,g115)
    c: InternalAlignment(g113,g115)
    c: InternalAlignment(g114,g115)
    c: InternalAlignment(g116,g115)
    c: InternalAlignment(g117,g115)
    c: Block(g109)
    c: Block(g115)
    c: Coincident(g118,g109)
    c: Coincident(g118,g115)
    c: Vertical(g118)
    c: Coincident(g119,g115)
    c: Coincident(g119,g73)
    c: Coincident(g120,g73)
    c: Coincident(g120,g109)
    c: Weight(g121) = 1
    c: Equal(g121,g122)
    c: Equal(g121,g123)
    c: InternalAlignment(g121,g124)
    c: InternalAlignment(g122,g124)
    c: InternalAlignment(g123,g124)
    c: InternalAlignment(g125,g124)
    c: InternalAlignment(g126,g124)
    c: Weight(g127) = 1
    c: Equal(g127,g128)
    c: Equal(g127,g129)
    c: InternalAlignment(g127,g130)
    c: InternalAlignment(g128,g130)
    c: InternalAlignment(g129,g130)
    c: InternalAlignment(g131,g130)
    c: InternalAlignment(g132,g130)
    c: Block(g124)
    c: Block(g130)
    c: Coincident(g133,g124)
    c: Coincident(g133,g130)
    c: Vertical(g133)
    c: Coincident(g134,g130)
    c: Coincident(g134,g67)
    c: Coincident(g135,g67)
    c: Coincident(g135,g124)
    c: Weight(g136) = 1
    c: Equal(g136,g137)
    c: Equal(g136,g138)
    c: InternalAlignment(g136,g139)
    c: InternalAlignment(g137,g139)
    c: InternalAlignment(g138,g139)
    c: InternalAlignment(g140,g139)
    c: InternalAlignment(g141,g139)
    c: Weight(g142) = 1
    c: Equal(g142,g143)
    c: Equal(g142,g144)
    c: InternalAlignment(g142,g145)
    c: InternalAlignment(g143,g145)
    c: InternalAlignment(g144,g145)
    c: InternalAlignment(g146,g145)
    c: InternalAlignment(g147,g145)
    c: Weight(g148) = 1
    c: Equal(g148,g149)
    c: Equal(g148,g150)
    c: InternalAlignment(g148,g151)
    c: InternalAlignment(g149,g151)
    c: InternalAlignment(g150,g151)
    c: InternalAlignment(g152,g151)
    c: InternalAlignment(g153,g151)
    c: Weight(g154) = 1
    c: Equal(g154,g155)
    c: Equal(g154,g156)
    c: InternalAlignment(g154,g157)
    c: InternalAlignment(g155,g157)
    c: InternalAlignment(g156,g157)
    c: InternalAlignment(g158,g157)
    c: InternalAlignment(g159,g157)
    c: Block(g157)
    c: Block(g151)
    c: Block(g145)
    c: Block(g139)
    c: Coincident(g160,g34)
    c: Coincident(g160,g157)
    c: Coincident(g161,g157)
    c: Coincident(g161,g151)
    c: Horizontal(g161)
    c: Coincident(g162,g151)
    c: Coincident(g162,g34)
    c: Vertical(g162)
    c: Coincident(g163,g28)
    c: Coincident(g163,g145)
    c: Vertical(g163)
    c: Coincident(g164,g145)
    c: Coincident(g164,g139)
    c: Horizontal(g164)
    c: Coincident(g165,g139)
    c: Coincident(g165,g28)
    c: Weight(g166) = 1
    c: Equal(g166,g167)
    c: Equal(g166,g168)
    c: InternalAlignment(g166,g169)
    c: InternalAlignment(g167,g169)
    c: InternalAlignment(g168,g169)
    c: InternalAlignment(g170,g169)
    c: InternalAlignment(g171,g169)
    c: Weight(g172) = 1
    c: Equal(g172,g173)
    c: Equal(g172,g174)
    c: InternalAlignment(g172,g175)
    c: InternalAlignment(g173,g175)
    c: InternalAlignment(g174,g175)
    c: InternalAlignment(g176,g175)
    c: InternalAlignment(g177,g175)
    c: Weight(g178) = 1
    c: Equal(g178,g179)
    c: Equal(g178,g180)
    c: InternalAlignment(g178,g181)
    c: InternalAlignment(g179,g181)
    c: InternalAlignment(g180,g181)
    c: InternalAlignment(g182,g181)
    c: InternalAlignment(g183,g181)
    c: Weight(g184) = 1
    c: Equal(g184,g185)
    c: Equal(g184,g186)
    c: InternalAlignment(g184,g187)
    c: InternalAlignment(g185,g187)
    c: InternalAlignment(g186,g187)
    c: InternalAlignment(g188,g187)
    c: InternalAlignment(g189,g187)
    c: Block(g187)
    c: Block(g181)
    c: Block(g175)
    c: Block(g169)
    c: Coincident(g190,g187)
    c: Coincident(g190,g181)
    c: Horizontal(g190)
    c: Coincident(g191,g181)
    c: Coincident(g191,g16)
    c: Vertical(g191)
    c: Coincident(g192,g22)
    c: Coincident(g192,g175)
    c: Vertical(g192)
    c: Coincident(g193,g175)
    c: Coincident(g193,g169)
    c: Horizontal(g193)
    c: Coincident(g194,g169)
    c: Coincident(g194,g22)
    c: Coincident(g195,g16)
    c: Weight(g196) = 1
    c: Equal(g196,g197)
    c: Equal(g196,g198)
    c: InternalAlignment(g196,g199)
    c: InternalAlignment(g197,g199)
    c: InternalAlignment(g198,g199)
    c: InternalAlignment(g200,g199)
    c: InternalAlignment(g201,g199)
    c: Weight(g202) = 1
    c: Equal(g202,g203)
    c: Equal(g202,g204)
    c: InternalAlignment(g202,g205)
    c: InternalAlignment(g203,g205)
    c: InternalAlignment(g204,g205)
    c: InternalAlignment(g206,g205)
    c: InternalAlignment(g207,g205)
    c: Block(g205)
    c: Block(g199)
    c: Coincident(g208,g205)
    c: Coincident(g208,g40)
    c: Coincident(g209,g40)
    c: Coincident(g209,g199)
    c: Coincident(g210,g199)
    c: Coincident(g210,g205)
    c: Vertical(g210)
    c: Weight(g211) = 1
    c: Equal(g211,g212)
    c: Equal(g211,g213)
    c: InternalAlignment(g211,g214)
    c: InternalAlignment(g212,g214)
    c: InternalAlignment(g213,g214)
    c: InternalAlignment(g215,g214)
    c: InternalAlignment(g216,g214)
    c: Weight(g217) = 1
    c: Equal(g217,g218)
    c: Equal(g217,g219)
    c: InternalAlignment(g217,g220)
    c: InternalAlignment(g218,g220)
    c: InternalAlignment(g219,g220)
    c: InternalAlignment(g221,g220)
    c: InternalAlignment(g222,g220)
    c: Block(g220)
    c: Block(g214)
    c: Coincident(g223,g214)
    c: Coincident(g223,g46)
    c: Coincident(g224,g46)
    c: Coincident(g224,g220)
    c: Coincident(g225,g220)
    c: Coincident(g225,g214)
    c: Vertical(g225)
    c: Horizontal(g226)
    c: Block(g226)
    c: Vertical(g227)
    c: Block(g227)
    c: Block(g228)
    c: Weight(g229) = 1
    c: Equal(g229,g230)
    c: Equal(g229,g231)
    c: InternalAlignment(g229,g232)
    c: InternalAlignment(g230,g232)
    c: InternalAlignment(g231,g232)
    c: InternalAlignment(g233,g232)
    c: InternalAlignment(g234,g232)
    c: Weight(g235) = 1
    c: Equal(g235,g236)
    c: Equal(g235,g237)
    c: InternalAlignment(g235,g238)
    c: InternalAlignment(g236,g238)
    c: InternalAlignment(g237,g238)
    c: InternalAlignment(g239,g238)
    c: InternalAlignment(g240,g238)
    c: Weight(g241) = 1
    c: Equal(g241,g242)
    c: Equal(g241,g243)
    c: InternalAlignment(g241,g244)
    c: InternalAlignment(g242,g244)
    c: InternalAlignment(g243,g244)
    c: InternalAlignment(g245,g244)
    c: InternalAlignment(g246,g244)
    c: Weight(g247) = 1
    c: Equal(g247,g248)
    c: Equal(g247,g249)
    c: InternalAlignment(g247,g250)
    c: InternalAlignment(g248,g250)
    c: InternalAlignment(g249,g250)
    c: InternalAlignment(g251,g250)
    c: InternalAlignment(g252,g250)
    c: Block(g232)
    c: Block(g238)
    c: Block(g244)
    c: Block(g250)
    c: Coincident(g253,g238)
    c: Coincident(g253,g232)
    c: Horizontal(g253)
    c: Block(g195)
    c: Weight(g254) = 1
    c: Equal(g254,g255)
    c: Equal(g254,g256)
    c: InternalAlignment(g254,g257)
    c: InternalAlignment(g255,g257)
    c: InternalAlignment(g256,g257)
    c: InternalAlignment(g258,g257)
    c: InternalAlignment(g259,g257)
    c: Weight(g260) = 1
    c: Equal(g260,g261)
    c: Equal(g260,g262)
    c: InternalAlignment(g260,g263)
    c: InternalAlignment(g261,g263)
    c: InternalAlignment(g262,g263)
    c: InternalAlignment(g264,g263)
    c: InternalAlignment(g265,g263)
    c: Weight(g266) = 1
    c: Equal(g266,g267)
    c: Equal(g266,g268)
    c: InternalAlignment(g266,g269)
    c: InternalAlignment(g267,g269)
    c: InternalAlignment(g268,g269)
    c: InternalAlignment(g270,g269)
    c: InternalAlignment(g271,g269)
    c: Block(g257)
    c: Block(g263)
    c: Block(g269)
    c: Coincident(g344,g257)
    c: Coincident(g272,g257)
    c: Coincident(g272,g263)
    c: Coincident(g273,g263)
    c: Vertical(g273)
    c: Weight(g274) = 1
    c: Equal(g274,g275)
    c: Equal(g274,g276)
    c: InternalAlignment(g274,g277)
    c: InternalAlignment(g275,g277)
    c: InternalAlignment(g276,g277)
    c: InternalAlignment(g278,g277)
    c: InternalAlignment(g279,g277)
    c: Weight(g280) = 1
    c: Equal(g280,g281)
    c: Equal(g280,g282)
    c: InternalAlignment(g280,g283)
    c: InternalAlignment(g281,g283)
    c: InternalAlignment(g282,g283)
    c: InternalAlignment(g284,g283)
    c: InternalAlignment(g285,g283)
    c: Weight(g286) = 1
    c: Equal(g286,g287)
    c: Equal(g286,g288)
    c: InternalAlignment(g286,g289)
    c: InternalAlignment(g287,g289)
    c: InternalAlignment(g288,g289)
    c: InternalAlignment(g290,g289)
    c: InternalAlignment(g291,g289)
    c: Block(g289)
    c: Block(g283)
    c: Block(g277)
    c: Coincident(g292,g283)
    c: Coincident(g292,g277)
    c: Coincident(g293,g277)
    c: Coincident(g293,g289)
    c: Vertical(g293)
    c: Coincident(g294,g289)
    c: Coincident(g294,g283)
    c: Horizontal(g294)
    c: Weight(g295) = 1
    c: Equal(g295,g296)
    c: InternalAlignment(g295,g297)
    c: InternalAlignment(g296,g297)
    c: InternalAlignment(g298,g297)
    c: InternalAlignment(g299,g297)
    c: Weight(g300) = 1
    c: Equal(g300,g301)
    c: Equal(g300,g302)
    c: InternalAlignment(g300,g303)
    c: InternalAlignment(g301,g303)
    c: InternalAlignment(g302,g303)
    c: InternalAlignment(g304,g303)
    c: InternalAlignment(g305,g303)
    c: Weight(g306) = 1
    c: Equal(g306,g307)
    c: Equal(g306,g308)
    c: InternalAlignment(g306,g309)
    c: InternalAlignment(g307,g309)
    c: InternalAlignment(g308,g309)
    c: InternalAlignment(g310,g309)
    c: InternalAlignment(g311,g309)
    c: Equal(g312,g313)
    c: Equal(g312,g314)
    c: InternalAlignment(g312,g315)
    c: InternalAlignment(g313,g315)
    c: InternalAlignment(g314,g315)
    c: InternalAlignment(g316,g315)
    c: InternalAlignment(g317,g315)
    c: Block(g303)
    c: Block(g309)
    c: Block(g315)
    c: Block(g297)
    c: Coincident(g318,g297)
    c: Coincident(g318,g303)
    c: Horizontal(g318)
    c: Coincident(g319,g303)
    c: Coincident(g319,g309)
    c: Vertical(g319)
    c: Coincident(g320,g309)
    c: Coincident(g320,g315)
    c: Horizontal(g320)
    c: Coincident(g321,g315)
    c: Coincident(g321,g297)
    c: Weight(g322) = 1
    c: Equal(g322,g323)
    c: Equal(g322,g324)
    c: InternalAlignment(g322,g325)
    c: InternalAlignment(g323,g325)
    c: InternalAlignment(g324,g325)
    c: InternalAlignment(g326,g325)
    c: InternalAlignment(g327,g325)
    c: Weight(g328) = 1
    c: Equal(g328,g329)
    c: Equal(g328,g330)
    c: InternalAlignment(g328,g331)
    c: InternalAlignment(g329,g331)
    c: InternalAlignment(g330,g331)
    c: InternalAlignment(g332,g331)
    c: InternalAlignment(g333,g331)
    c: Weight(g334) = 1
    c: Equal(g334,g335)
    c: Equal(g334,g336)
    c: InternalAlignment(g334,g337)
    c: InternalAlignment(g335,g337)
    c: InternalAlignment(g336,g337)
    c: InternalAlignment(g338,g337)
    c: InternalAlignment(g339,g337)
    c: Block(g337)
    c: Block(g331)
    c: Block(g325)
    c: Coincident(g340,g337)
    c: Coincident(g340,g331)
    c: Horizontal(g340)
    c: Coincident(g341,g331)
    c: Coincident(g341,g325)
    c: Vertical(g341)
    c: Coincident(g342,g325)
    c: Coincident(g342,g337)
    c: Block(g343)
    c: Coincident(g344,g343)
    c: Coincident(g273,g343)
    c: Horizontal(g345)
    c: Distance(g345) = 4
    c: Coincident(g345,g273)
    c: InternalAlignment(g346,g347)
    c: InternalAlignment(g348,g347)
    c: InternalAlignment(g349,g347)
    c: Block(g347)
    c: Coincident(g349,g345)
    c: Horizontal(g350)
    c: Distance(g350) = 4
FEATURE [Sketcher::SketchObject] Sketch001
  FullyConstrained = true
  MapMode = 4
  Placement = pos=(0,0,0) rot=(0.57735,0.57735,0.57735;2.0944rad)
  Support = -> [Sketch]
  sketch-geometry (46):
    g0: BSplineCurve PolesCount=3 KnotsCount=2 Degree=2 IsPeriodic=0
    g1: ArcOfCircle CenterX=73.1223 CenterY=-32.291 CenterZ=0 NormalX=0 NormalY=0 NormalZ=1 AngleXU=0 Radius=13 StartAngle=5.92268 EndAngle=9.06428
    g2: ArcOfCircle CenterX=66.7816 CenterY=-49.1439 CenterZ=0 NormalX=0 NormalY=0 NormalZ=1 AngleXU=0 Radius=13 StartAngle=2.78068 EndAngle=5.92131
    g3: ArcOfCircle CenterX=55.9263 CenterY=-78.1807 CenterZ=0 NormalX=0 NormalY=0 NormalZ=1 AngleXU=0 Radius=13 StartAngle=5.92268 EndAngle=9.06428
    g4: ArcOfCircle CenterX=49.5884 CenterY=-95.0342 CenterZ=0 NormalX=0 NormalY=0 NormalZ=1 AngleXU=0 Radius=13 StartAngle=2.78068 EndAngle=5.92131
    g5: ArcOfCircle CenterX=38.7206 CenterY=-124.067 CenterZ=0 NormalX=0 NormalY=0 NormalZ=1 AngleXU=0 Radius=13 StartAngle=5.92268 EndAngle=9.06428
    g6: ArcOfCircle CenterX=32.3875 CenterY=-140.92 CenterZ=0 NormalX=0 NormalY=0 NormalZ=1 AngleXU=0 Radius=13 StartAngle=2.78068 EndAngle=5.92131
    g7: ArcOfCircle CenterX=21.4715 CenterY=-169.934 CenterZ=0 NormalX=0 NormalY=0 NormalZ=1 AngleXU=0 Radius=13 StartAngle=5.92268 EndAngle=9.06428
    g8: ArcOfCircle CenterX=15.1336 CenterY=-186.787 CenterZ=0 NormalX=0 NormalY=0 NormalZ=1 AngleXU=0 Radius=13 StartAngle=2.78068 EndAngle=5.92131
    g9-g12: Circle x4 (B-spline internal-alignment scaffolding for g13; pole/knot coordinates omitted)
    g13: BSplineCurve PolesCount=4 KnotsCount=2 Degree=3 IsPeriodic=0
    g14: GeomPoint X=28.8094 Y=-19.0875 Z=0
    g15: GeomPoint X=47.0443 Y=-50.4712 Z=0
    g16: Circle CenterX=53.5586 CenterY=-23.2695 CenterZ=0 NormalX=0 NormalY=0 NormalZ=1 AngleXU=0 Radius=3.24518
    g17: Circle CenterX=-195.441 CenterY=-127.082 CenterZ=0 NormalX=0 NormalY=0 NormalZ=1 AngleXU=0 Radius=1
    g18: Circle CenterX=-8.24091 CenterY=-197.481 CenterZ=0 NormalX=0 NormalY=0 NormalZ=1 AngleXU=0 Radius=1
    g19: Circle CenterX=12.8789 CenterY=-141.321 CenterZ=0 NormalX=0 NormalY=0 NormalZ=1 AngleXU=0 Radius=1
    g20: BSplineCurve PolesCount=3 KnotsCount=2 Degree=2 IsPeriodic=0
    g21: GeomPoint X=-195.441 Y=-127.082 Z=0
    g22: GeomPoint X=12.8789 Y=-141.321 Z=0
    g23: Circle CenterX=-12.8016 CenterY=-179.036 CenterZ=0 NormalX=0 NormalY=0 NormalZ=1 AngleXU=0 Radius=10.5072
    g24: Circle CenterX=0.933922 CenterY=-166.43 CenterZ=0 NormalX=0 NormalY=0 NormalZ=1 AngleXU=0 Radius=3.26661
    g25: Circle CenterX=-33.5518 CenterY=-176.44 CenterZ=0 NormalX=0 NormalY=0 NormalZ=1 AngleXU=0 Radius=5.64388
    g26: Circle CenterX=-47.2366 CenterY=-173.859 CenterZ=0 NormalX=0 NormalY=0 NormalZ=1 AngleXU=0 Radius=3.01653
    g27: Circle CenterX=-56.2595 CenterY=-171.456 CenterZ=0 NormalX=0 NormalY=0 NormalZ=1 AngleXU=0 Radius=2.12826
    g28: ArcOfCircle CenterX=51.2151 CenterY=-198.473 CenterZ=0 NormalX=0 NormalY=0 NormalZ=1 AngleXU=0 Radius=20 StartAngle=2.78189 EndAngle=4.35269
    g29: LineSegment StartX=32.4951 StartY=-191.433 StartZ=0 EndX=94.6578 EndY=-26.1352 EndZ=0
    g30: LineSegment StartX=43.1192 StartY=-220.001 StartZ=0 EndX=-196.497 EndY=-129.89 EndZ=0
    g31: LineSegment StartX=43.1192 StartY=-220.001 StartZ=0 EndX=44.1752 EndY=-217.193 EndZ=0
    g32: LineSegment StartX=117.223 StartY=-19.0875 StartZ=0 EndX=117.223 EndY=-16.0875 EndZ=0
    g33: LineSegment StartX=117.223 StartY=-16.0875 StartZ=0 EndX=17.2232 EndY=-16.0875 EndZ=0
    g34: LineSegment StartX=17.2232 StartY=-16.0875 StartZ=0 EndX=17.2232 EndY=-19.0875 EndZ=0
    g35: LineSegment StartX=28.8094 StartY=-19.0875 StartZ=0 EndX=17.2232 EndY=-19.0875 EndZ=0
    g36: LineSegment StartX=47.0443 StartY=-50.4712 StartZ=0 EndX=12.8789 EndY=-141.321 EndZ=0
    g37: LineSegment StartX=-195.441 StartY=-127.082 StartZ=0 EndX=-196.497 EndY=-129.89 EndZ=0
    g38: LineSegment StartX=85.2866 StartY=-36.8766 StartZ=0 EndX=78.9396 EndY=-53.7463 EndZ=0
    g39: LineSegment StartX=60.9579 StartY=-27.7053 StartZ=0 EndX=54.6191 EndY=-44.5532 EndZ=0
    g40: LineSegment StartX=68.0907 StartY=-82.7664 StartZ=0 EndX=61.7465 EndY=-99.6365 EndZ=0
    g41: LineSegment StartX=43.7619 StartY=-73.595 StartZ=0 EndX=37.426 EndY=-90.4435 EndZ=0
    g42: LineSegment StartX=50.885 StartY=-128.652 StartZ=0 EndX=44.5456 EndY=-145.522 EndZ=0
    g43: LineSegment StartX=26.5562 StartY=-119.481 StartZ=0 EndX=20.2251 EndY=-136.329 EndZ=0
    g44: LineSegment StartX=9.3071 StartY=-165.349 StartZ=0 EndX=2.97115 EndY=-182.197 EndZ=0
    g45: LineSegment StartX=33.6358 StartY=-174.52 StartZ=0 EndX=27.2917 EndY=-191.39 EndZ=0
  constraints (71):
    c: Block(g0)
    c: Block(g1)
    c: Block(g2)
    c: Block(g4)
    c: Block(g3)
    c: Block(g6)
    c: Block(g5)
    c: Block(g8)
    c: Block(g7)
    c: Weight(g9) = 1
    c: Equal(g9,g10)
    c: Equal(g9,g11)
    c: Equal(g9,g12)
    c: InternalAlignment(g9-g12 -> g13) x4
    c: InternalAlignment(g14,g13)
    c: InternalAlignment(g15,g13)
    c: Block(g16)
    c: Weight(g17) = 1
    c: Equal(g17,g18)
    c: Equal(g17,g19)
    c: InternalAlignment(g17,g20)
    c: InternalAlignment(g18,g20)
    c: InternalAlignment(g19,g20)
    c: InternalAlignment(g21,g20)
    c: InternalAlignment(g22,g20)
    c: Block(g20)
    c: Block(g23)
    c: Block(g24)
    c: Block(g25)
    c: Block(g26)
    c: Block(g27)
    c: Block(g28)
    c: Coincident(g29,g28)
    c: Coincident(g29,g0)
    c: Block(g13)
    c: Coincident(g31,g30)
    c: Coincident(g31,g28)
    c: Block(g31)
    c: Coincident(g32,g0)
    c: Vertical(g32)
    c: Coincident(g33,g32)
    c: Horizontal(g33)
    c: Coincident(g34,g33)
    c: Vertical(g34)
    c: Block(g33)
    c: Coincident(g35,g13)
    c: Coincident(g35,g34)
    c: Horizontal(g35)
    c: Coincident(g36,g13)
    c: Coincident(g36,g20)
    c: Coincident(g37,g20)
    c: Coincident(g37,g30)
    c: Block(g30)
    c: Coincident(g38,g1)
    c: Coincident(g38,g2)
    c: Coincident(g39,g1)
    c: Coincident(g39,g2)
    c: Coincident(g40,g3)
    c: Coincident(g40,g4)
    c: Coincident(g41,g3)
    c: Coincident(g41,g4)
    c: Coincident(g42,g5)
    c: Coincident(g42,g6)
    c: Coincident(g43,g5)
    c: Coincident(g43,g6)
    c: Coincident(g44,g7)
    c: Coincident(g44,g8)
    c: Coincident(g45,g7)
    c: Coincident(g45,g8)
    c: Distance(g30) = 256
    c: Distance(g33) = 100
FEATURE [Part::Extrusion] Extrude002
  Base = -> Sketch001
  Dir = (1,0,0)
  DirMode = 2
  FaceMakerClass = Part::FaceMakerBullseye
  LengthFwd = 8
  LengthRev = 0
  Solid = true
  Symmetric = false
FEATURE [Sketcher::SketchObject] Sketch002
  FullyConstrained = true
  sketch-geometry (20):
    g0: LineSegment StartX=-2.77179 StartY=-200.304 StartZ=0 EndX=5.22821 EndY=-200.304 EndZ=0
    g1: LineSegment StartX=5.22821 StartY=-200.304 StartZ=0 EndX=5.22821 EndY=-197.304 EndZ=0
    g2: LineSegment StartX=-2.77179 StartY=-200.304 StartZ=0 EndX=-2.77179 EndY=-197.304 EndZ=0
    g3: LineSegment StartX=5.22821 StartY=-197.304 StartZ=0 EndX=8.22821 EndY=-197.304 EndZ=0
    g4: LineSegment StartX=-2.77179 StartY=-197.304 StartZ=0 EndX=-5.77179 EndY=-197.304 EndZ=0
    g5: LineSegment StartX=19.2282 StartY=-203.304 StartZ=0 EndX=19.2282 EndY=-206.304 EndZ=0
    g6: LineSegment StartX=-16.7718 StartY=-203.304 StartZ=0 EndX=-16.7718 EndY=-206.304 EndZ=0
    g7: LineSegment StartX=-16.7718 StartY=-206.304 StartZ=0 EndX=19.2282 EndY=-206.304 EndZ=0
    g8: Circle CenterX=-16.7718 CenterY=-203.304 CenterZ=0 NormalX=0 NormalY=0 NormalZ=1 AngleXU=0 Radius=1
    g9: Circle CenterX=-5.77179 CenterY=-203.304 CenterZ=0 NormalX=0 NormalY=0 NormalZ=1 AngleXU=0 Radius=1
    g10: Circle CenterX=-5.77179 CenterY=-197.304 CenterZ=0 NormalX=0 NormalY=0 NormalZ=1 AngleXU=0 Radius=1
    g11: BSplineCurve PolesCount=3 KnotsCount=2 Degree=2 IsPeriodic=0
    g12: GeomPoint X=-16.7718 Y=-203.304 Z=0
    g13: GeomPoint X=-5.77179 Y=-197.304 Z=0
    g14: Circle CenterX=19.2282 CenterY=-203.304 CenterZ=0 NormalX=0 NormalY=0 NormalZ=1 AngleXU=0 Radius=1
    g15: Circle CenterX=8.22821 CenterY=-203.304 CenterZ=0 NormalX=0 NormalY=0 NormalZ=1 AngleXU=0 Radius=1
    g16: Circle CenterX=8.22821 CenterY=-197.304 CenterZ=0 NormalX=0 NormalY=0 NormalZ=1 AngleXU=0 Radius=1
    g17: BSplineCurve PolesCount=3 KnotsCount=2 Degree=2 IsPeriodic=0
    g18: GeomPoint X=19.2282 Y=-203.304 Z=0
    g19: GeomPoint X=8.22821 Y=-197.304 Z=0
  constraints (41):
    c: Horizontal(g0)
    c: Distance(g0) = 8
    c: Coincident(g1,g0)
    c: Vertical(g1)
    c: Distance(g1) = 3
    c: Coincident(g2,g0)
    c: Vertical(g2)
    c: Distance(g2) = 3
    c: Coincident(g3,g1)
    c: Horizontal(g3)
    c: Distance(g3) = 3
    c: Coincident(g4,g2)
    c: Horizontal(g4)
    c: Distance(g4) = 3
    c: Vertical(g5)
    c: Vertical(g6)
    c: Coincident(g7,g6)
    c: Coincident(g7,g5)
    c: Weight(g8) = 1
    c: Equal(g8,g9)
    c: Equal(g8,g10)
    c: Coincident(g11,g4)
    c: InternalAlignment(g8,g11)
    c: InternalAlignment(g9,g11)
    c: InternalAlignment(g10,g11)
    c: InternalAlignment(g12,g11)
    c: InternalAlignment(g13,g11)
    c: Coincident(g17,g5)
    c: Weight(g14) = 1
    c: Equal(g14,g15)
    c: Equal(g14,g16)
    c: Coincident(g17,g3)
    c: InternalAlignment(g14,g17)
    c: InternalAlignment(g15,g17)
    c: InternalAlignment(g16,g17)
    c: InternalAlignment(g18,g17)
    c: InternalAlignment(g19,g17)
    c: Block(g7)
    c: Block(g17)
    c: Block(g11)
    c: Block(g6)
FEATURE [Part::Extrusion] Extrude003
  Base = -> Sketch002
  Dir = (0,0,1)
  DirMode = 2
  FaceMakerClass = Part::FaceMakerBullseye
  LengthFwd = 260
  LengthRev = 0
  Solid = true
  Symmetric = false
FEATURE [Part::Extrusion] Extrude
  Base = -> Sketch
  Dir = (0,0,1)
  DirMode = 2
  FaceMakerClass = Part::FaceMakerBullseye
  LengthFwd = 14
  LengthRev = 0
  Solid = true
  Symmetric = false
